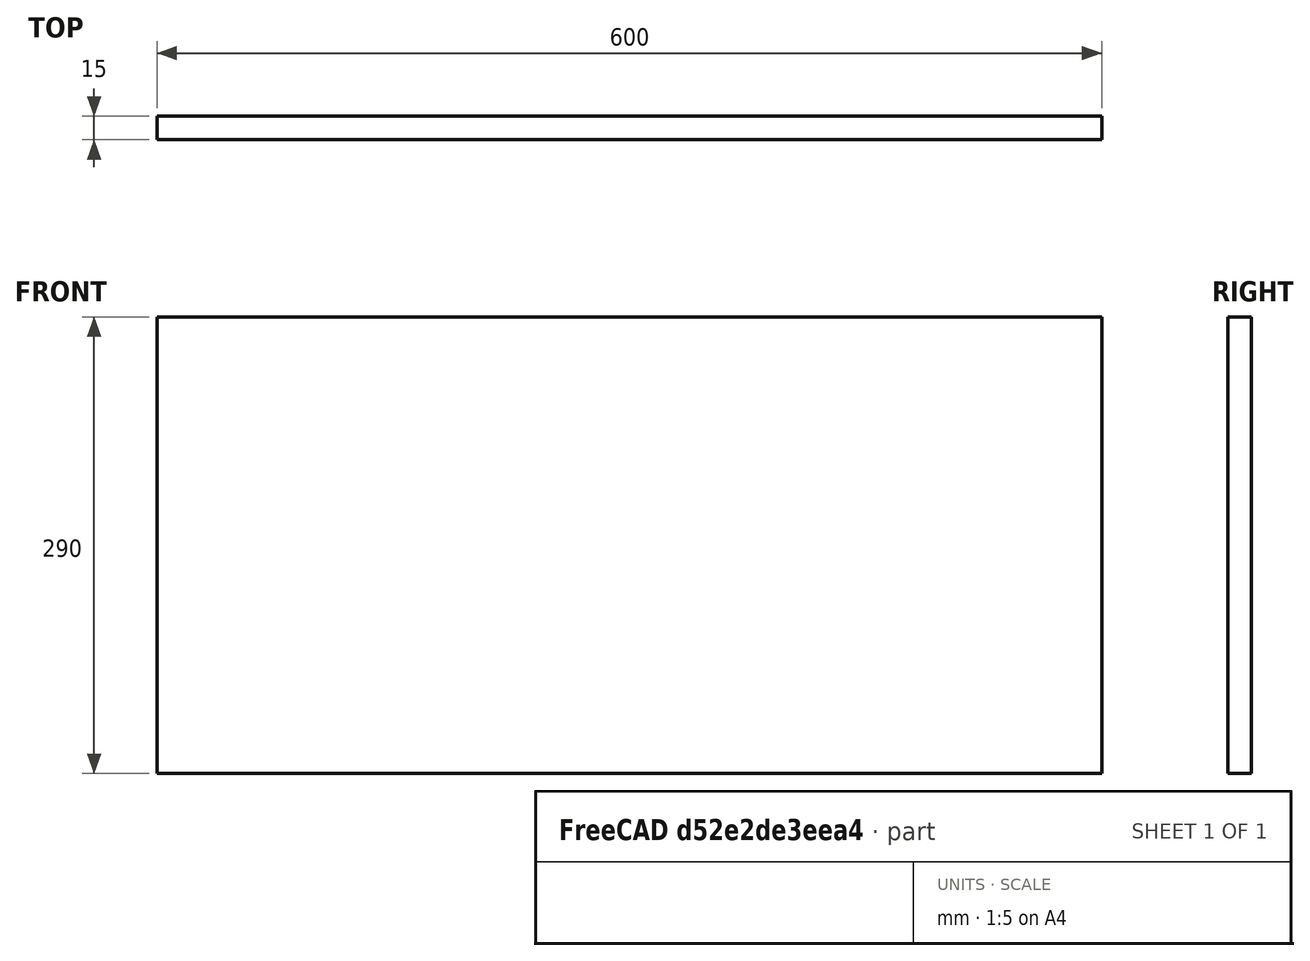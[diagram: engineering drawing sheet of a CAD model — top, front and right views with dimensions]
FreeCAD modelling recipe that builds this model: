
FCSTD DOCUMENT  (FreeCAD 1.0R39319 (Git))
Label: back_bottom
License: All rights reserved
LicenseURL: https://en.wikipedia.org/wiki/All_rights_reserved
objects: Sketcher::SketchObject×1, PartDesign::Pad×1, PartDesign::Body×1
note: 6 computed .brp shape members not serialized (recipe doc carries the construction recipe); baked Part::Feature solids carry a one-line shape summary decoded from their .brp

FEATURE [Sketcher::SketchObject] Sketch  label="back_bottom_s"
  ArcFitTolerance = 1e-06
  AttachmentSupport = -> [XZ_Plane]
  FullyConstrained = true
  MakeInternals = false
  MapMode = 5
  Placement = pos=(0,0,0) rot=(1,0,0;1.5708rad)
  sketch-geometry (4):
    g0: LineSegment StartX=0 StartY=0 StartZ=0 EndX=600 EndY=0 EndZ=0
    g1: LineSegment StartX=600 StartY=0 StartZ=0 EndX=600 EndY=290 EndZ=0
    g2: LineSegment StartX=600 StartY=290 StartZ=0 EndX=0 EndY=290 EndZ=0
    g3: LineSegment StartX=0 StartY=290 StartZ=0 EndX=0 EndY=0 EndZ=0
  constraints (11):
    c: Coincident(g0,g1)
    c: Coincident(g1,g2)
    c: Coincident(g2,g3)
    c: Coincident(g3,g0)
    c: Horizontal(g0)
    c: Horizontal(g2)
    c: Vertical(g1)
    c: Vertical(g3)
    c: Coincident(g0,g-1)
    c: DistanceX(g2,g2) = 600
    c: DistanceY(g3,g3) = 290
FEATURE [PartDesign::Pad] Pad  label="back_bottom"
  Direction = (0,-1,2e-16)
  Length = 15
  Length2 = 10
  Placement = pos=(0,0,0) rot=(1,0,0;1.5708rad)
  Profile = -> Sketch
  ReferenceAxis = -> Sketch [N_Axis]
  Refine = true
  Suppressed = false
  Type = 0
FEATURE [PartDesign::Body] Body  label="back_bottom_body"
  AllowCompound = false
  Group = -> [Sketch,Pad]
  Origin = -> Origin
  Tip = -> Pad
